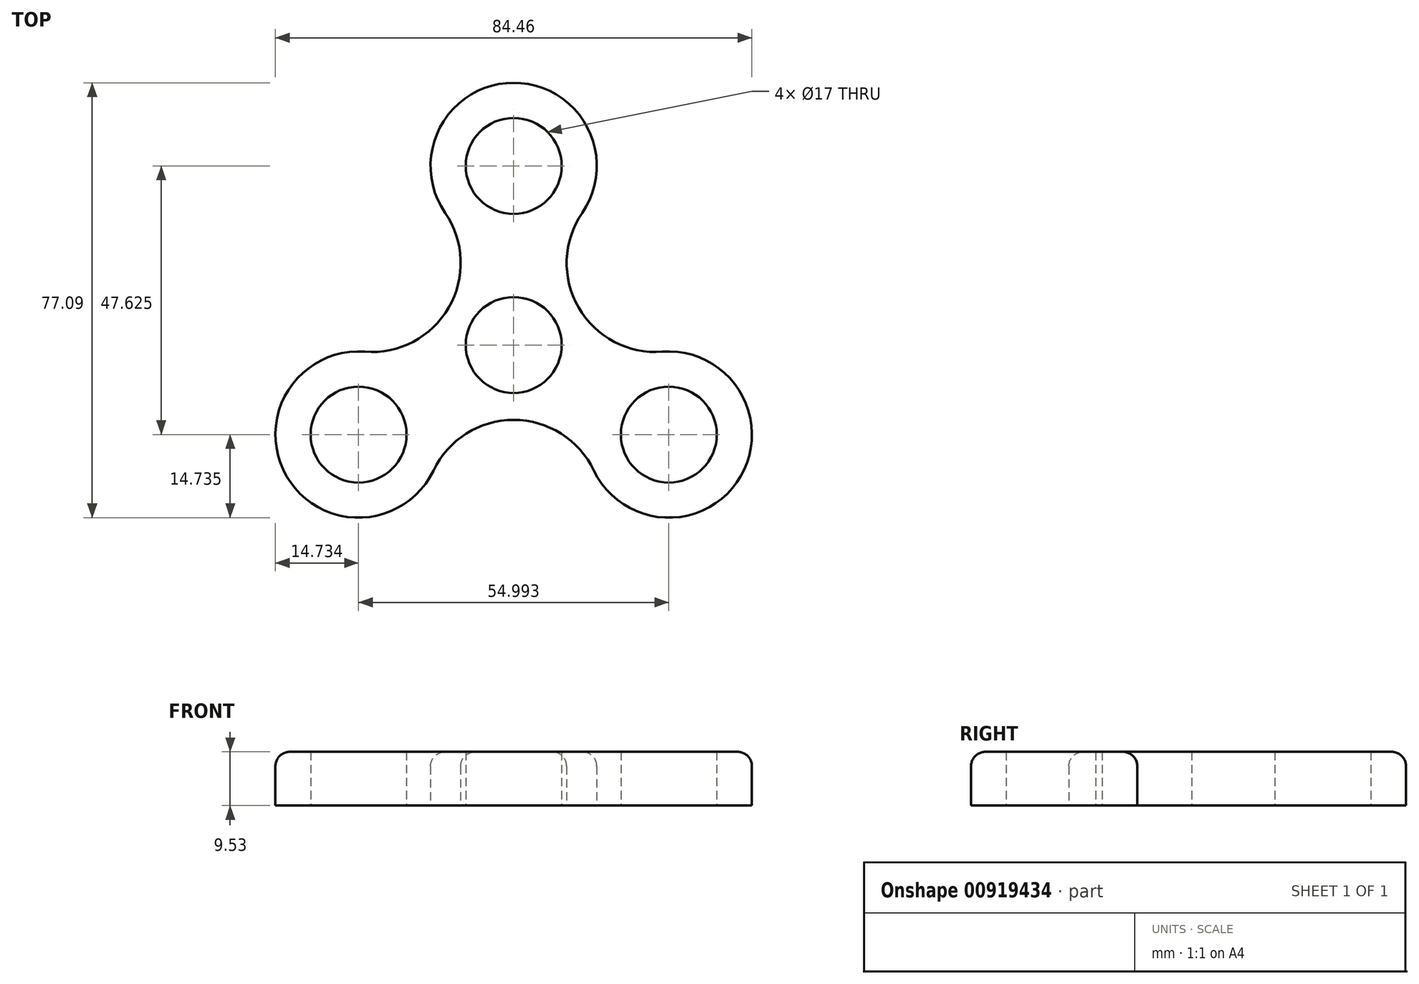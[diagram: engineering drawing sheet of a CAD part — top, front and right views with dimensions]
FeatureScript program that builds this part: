
annotation { "Feature Type Name" : "Feature", "Feature Type Description" : "" }
export const myFeature = defineFeature(function(context is Context, id is Id, definition is map)
    precondition{}
    {
        {
            var Q0;
            Q0=qCreatedBy(makeId("Top.planeOp"),FACE);
            var sketch = newSketch(context, id + "F0", { "sketchPlane" : qUnion([Q0])});
            skCircle(sketch, "E0", {"center": v(0, 0) * mm, "radius": 8.5 * mm});
            skCircle(sketch, "E1", {"center": v(0, 31.75) * mm, "radius": 8.5 * mm});
            skCircle(sketch, "E2.1.0", {"center": v(-27.5, -15.87) * mm, "radius": 8.5 * mm});
            skArc(sketch, "E2.1.1", {"start": v(-26.36, -1.19) * mm, "mid": v(-40.25, -23.24) * mm, "end": v(-14.2, -22.23) * mm});
            skCircle(sketch, "E2.2.0", {"center": v(27.5, -15.87) * mm, "radius": 8.5 * mm});
            skArc(sketch, "E2.2.1", {"start": v(14.2, -22.23) * mm, "mid": v(40.25, -23.24) * mm, "end": v(26.36, -1.19) * mm});
            skArc(sketch, "E3", {"start": v(-26.36, -1.19) * mm, "mid": v(-11.5, 6.64) * mm, "end": v(-12.15, 23.42) * mm});
            skArc(sketch, "E4", {"start": v(12.15, 23.42) * mm, "mid": v(11.5, 6.64) * mm, "end": v(26.36, -1.19) * mm});
            skArc(sketch, "E5", {"start": v(14.2, -22.23) * mm, "mid": v(0, -13.28) * mm, "end": v(-14.2, -22.23) * mm});
            skCircle(sketch, "E6", {"center": v(0, 0) * mm, "radius": 31.75 * mm, "construction": true});
            skArc(sketch, "E7", {"start": v(12.15, 23.42) * mm, "mid": v(0, 46.48) * mm, "end": v(-12.15, 23.42) * mm});
            skSolve(sketch);
        }
        {
            var Q0;
            Q0=makeQuery(id+"F0.imprint","IMPRINT",FACE,{"disambiguationData":[TD([[makeQuery(id+"F0.imprint","IMPRINT",EDGE,{"derivedFrom":sQuery(id+"F0.wireOp",EDGE,"E0")}),-1.0]])]});
            extrude(context, id + "F1", {"entities" : qUnion([Q0]), "depth" : 9.52 * mm, "offsetDistance" : 25.4 * mm});
        }
        {
            var Q0;
            Q0=makeQuery(id+"F1.opExtrude","CAP_EDGE",EDGE,{"disambiguationData":[OSD([sQuery(id+"F0.wireOp",EDGE,"E3")])],"isStart":false});
            var Q1;
            Q1=makeQuery(id+"F1.opExtrude","CAP_EDGE",EDGE,{"disambiguationData":[OSD([sQuery(id+"F0.wireOp",EDGE,"2IjanIbB-e7p6-vh6Q-00nR-2uLGs1TVL8rA")])],"isStart":true});
            fillet(context, id + "F2", {"entities" : qUnion([Q0, Q1]), "radius" : 2.54 * mm, "tangentPropagation" : true, "defaultsChanged" : false, "allowEdgeOverflow" : false, "vertexSettings" : []});
        }
    });
